# Revit family: Double_Check_Detector_Assemblies-Backflow_Prevention-WATTS-007DCDA_Series
name_source: partatom
category: Pipe Accessories
units: mm (PartAtom-declared; Revit-internal decimal feet)

## family parameters
Always vertical = Yes
Cut with Voids When Loaded = No
OmniClass Number = 23.65.55.14.21
OmniClass Title = Non-Return Valves for Liquid Services
Part Type = Valve - Breaks Into
Round Connector Dimension = Use Radius
Shared = No
Work Plane-Based = No

## types (2) — shared parameters
Assembly Code = F1050
BP_Dist1 = 6 13/16"
BP_Dist2 = 10 5/8"
BP_Hieght = 4 21/32"
BP_Length = 21 1/2"
BP_Rad = 1/2"
BP_Short_Length = 8 13/16"
BP_Sweep_Rad = 9/16"
BP_WM_Btm = 1 17/32"
BP_WM_Dist = 7/32"
BP_WM_Rad = 2"
BP_WM_Top = 2 15/16"
CHK_Body_Large_Rad = 2 11/16"
CHK_Body_Small_Rad = 2"
CHK_Flange_Rad = 3 3/4"
CHK_Flange_Thk = 3/4"
CHK_In_1st_Angle = 3 5/32"
CHK_In_2nd_Angle = 14 19/32"
CHK_In_RV = 8 25/32"
CL_TC1 = 4 3/16"
CL_TC3 = 1 3/4"
CW Connection = Yes
Connection Size = 2 1/2"
Connection Type = Flange
Country = United States
Description = Series 007DCDA Double Check Detector Assemblies prevent the backflow of non-health hazard fire protection system substances from being pumped or siphoned into the potable water supply. It incorporates a meter to detect ground leaks and unauthorized illegal taps, greatly reducing annual water expenses. Its compact epoxy coated cast iron unibody and modular check design facilitate simple and easy installation and maintenance. Maximum Working Pressure: 175psi (12.06 bar).
Flow Rate = 7.5 fps / 2.3 mps
GV_Bonnet_Angle = 45.00°
GV_Flange_Thk = 9/16"
GV_Handle_Thk = 3/4"
GV_Out_Flg_Ext = -9/16"
HW Connection = No
Installation Instructions = http://www.watts.com
Manufacturer = WATTS
Manufacturer Product Line = Backflow Prevention
Material = Metal-Watts-Epoxy Coated Cast Iron
Model = 007DCDA-OSY
Pressure Rating = 180 psi
Product Documentation Link = http://media.wattswater.com
Product Page URL = http://www.watts.com
RV_Cover_Boss_Angle = 45.00°
RV_Cover_Boss_Hieght = 5 1/2"
RV_Cover_Boss_Large_Rad = 1 1/8"
RV_Cover_Boss_Small_Rad = 5/8"
RV_Cover_Hieght = 4 1/2"
RV_Cover_Rad = 3 7/8"
RV_Cover_Thk = 1 9/16"
RV_Main_Dist = 2 31/32"
RV_Port_Dist = 4 3/16"
RV_Port_Rad = 1 9/32"
RV_Rad = 2 15/16"
Region = North America
Revised Date = 1/11/2016
TC2_Boss_Hieght = 3 9/16"
TC2_Dist = 1 15/32"
TC2_Hieght = 8 3/16"
TC3_Dist = 3 31/32"
TC3_Hieght = 5 1/4"
TC4_Boss_Hieght = 3 3/32"
TC4_Dist = 14 5/32"
TC4_Hieght = 8 3/16"
TC_Body_Length = 2 1/16"
TC_Body_Rad = 21/32"
TC_Boss_Rad = 13/16"
TC_Nipple_Rad = 1/2"
URL = http://www.watts.com
VALVE_OAL = 18 1/8"
Vent Connection = No
Waste Connection = No
Width = 12 5/16"

## per-type parameters (varying)
| type | Connection Inlet Description | Connection Outlet Description | Connection_Rad | GV_Bonnet_Height | GV_Flange_Rad | GV_Flow_Rad | GV_Handle_Height | GV_Handle_Rad | GV_OAL | GV_OSY_Stem_Hieght | GV_Stem_Dist | GV_Stem_Rad | Height | Length | Nominal Length | Ordering Code | Shipping Weight |
| 007DCDA - 2.5" | 2 1/2" Inlet Connection | 2 1/2" Outlet Connection | 1" | 8" | 3 1/2" | 1 19/32" | 13 3/4" | 3 5/8" | 7 1/2" | 2 13/16" | 3 3/4" | 7/16" | 16 3/8" | 33 1/4" | 16 3/8" | CFM Meter : 0062511 / GPM Meter : 0062510 | 160 lb |
| 007DCDA - 3" | 3" Inlet Connection | 3" Outlet Connection | 2" | 10" | 3 3/4" | 1 27/32" | 15 1/2" | 4" | 8" | 3 3/16" | 4" | 9/16" | 18 7/8" | 34 1/4" | 16 5/8" | CFM Meter : 0062513 / GPM Meter : 0062512 | 100 lb |

## geometry (parser evidence)
native form markers: Sweep x2
no freeform markers — native parametric forms only
